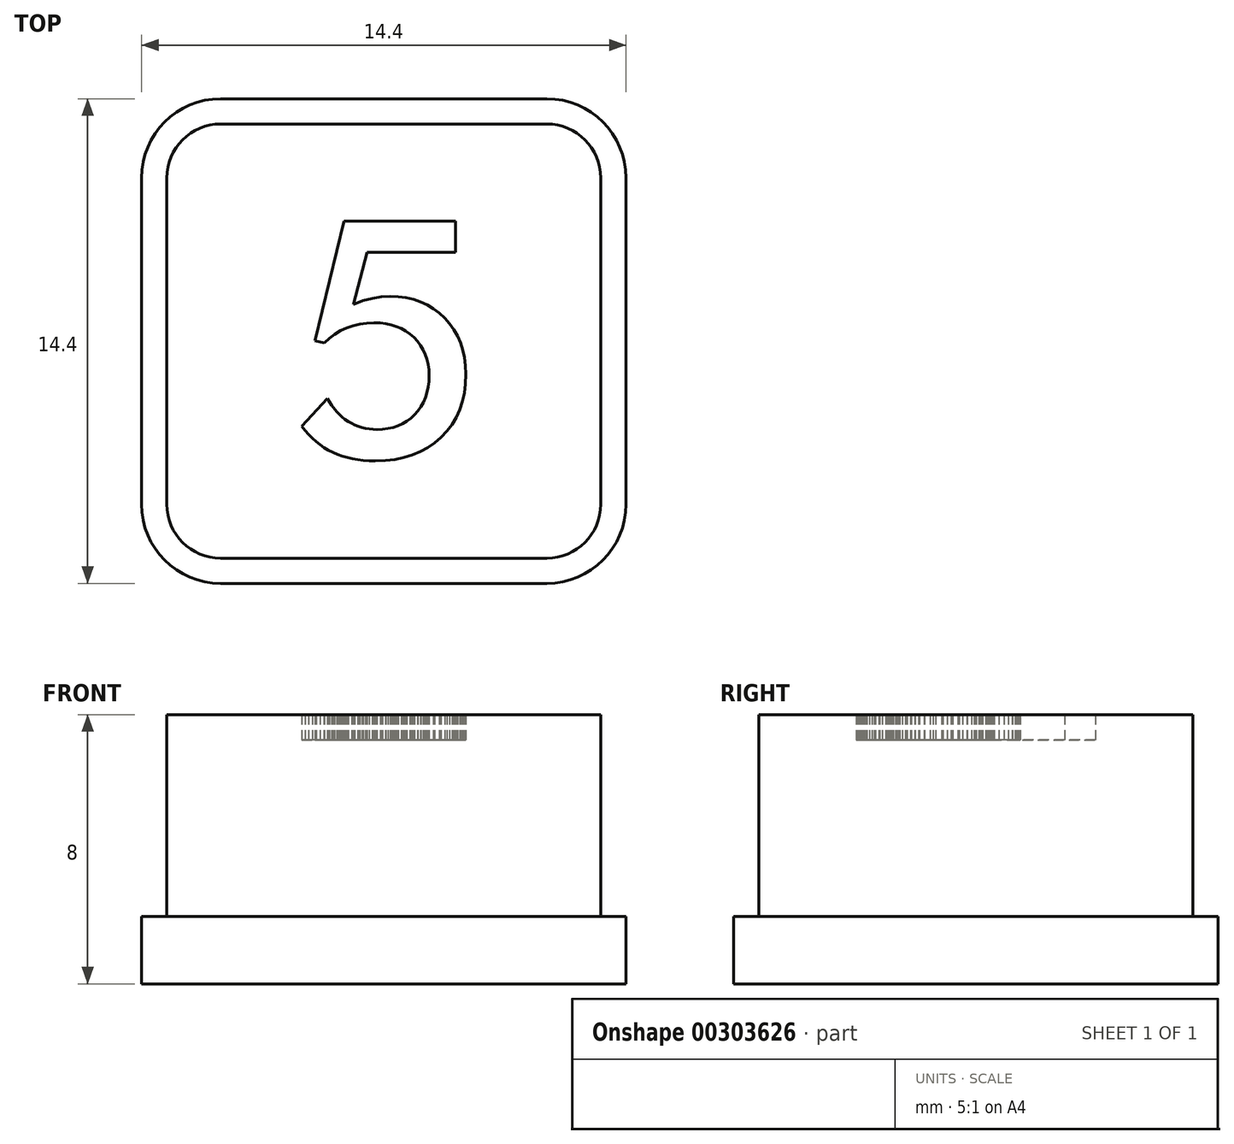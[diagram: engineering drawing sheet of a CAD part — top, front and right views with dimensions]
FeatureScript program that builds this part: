
annotation { "Feature Type Name" : "Feature", "Feature Type Description" : "" }
export const myFeature = defineFeature(function(context is Context, id is Id, definition is map)
    precondition{}
    {
        {
            var Q0;
            Q0=qCreatedBy(makeId("Top.planeOp"),FACE);
            var sketch = newSketch(context, id + "F0", { "sketchPlane" : qUnion([Q0])});
            skArc(sketch, "E0", {"start": v(4.85, -6.45) * mm, "mid": v(5.98, -5.98) * mm, "end": v(6.45, -4.85) * mm});
            skLineSegment(sketch, "E1", {"start": v(6.45, -4.85) * mm, "end": v(6.45, 4.85) * mm});
            skArc(sketch, "E2", {"start": v(6.45, 4.85) * mm, "mid": v(5.98, 5.98) * mm, "end": v(4.85, 6.45) * mm});
            skLineSegment(sketch, "E3", {"start": v(4.85, 6.45) * mm, "end": v(-4.85, 6.45) * mm});
            skArc(sketch, "E4", {"start": v(-4.85, 6.45) * mm, "mid": v(-5.98, 5.98) * mm, "end": v(-6.45, 4.85) * mm});
            skLineSegment(sketch, "E5", {"start": v(-6.45, 4.85) * mm, "end": v(-6.45, -4.85) * mm});
            skArc(sketch, "E6", {"start": v(-6.45, -4.85) * mm, "mid": v(-5.98, -5.98) * mm, "end": v(-4.85, -6.45) * mm});
            skLineSegment(sketch, "E7", {"start": v(-4.85, -6.45) * mm, "end": v(4.85, -6.45) * mm});
            skArc(sketch, "E8", {"start": v(-4.85, 7.2) * mm, "mid": v(-6.51, 6.51) * mm, "end": v(-7.2, 4.85) * mm});
            skLineSegment(sketch, "E9", {"start": v(-7.2, 4.85) * mm, "end": v(-7.2, -4.85) * mm});
            skArc(sketch, "E10", {"start": v(-7.2, -4.85) * mm, "mid": v(-6.51, -6.51) * mm, "end": v(-4.85, -7.2) * mm});
            skLineSegment(sketch, "E11", {"start": v(-4.85, -7.2) * mm, "end": v(4.85, -7.2) * mm});
            skArc(sketch, "E12", {"start": v(4.85, -7.2) * mm, "mid": v(6.51, -6.51) * mm, "end": v(7.2, -4.85) * mm});
            skLineSegment(sketch, "E13", {"start": v(7.2, -4.85) * mm, "end": v(7.2, 4.85) * mm});
            skArc(sketch, "E14", {"start": v(7.2, 4.85) * mm, "mid": v(6.51, 6.51) * mm, "end": v(4.85, 7.2) * mm});
            skLineSegment(sketch, "E15", {"start": v(4.85, 7.2) * mm, "end": v(-4.85, 7.2) * mm});
            skLineSegment(sketch, "E16", {"start": v(-1.68, -1.7) * mm, "end": v(-1.55, -1.91) * mm});
            skLineSegment(sketch, "E17", {"start": v(-1.55, -1.91) * mm, "end": v(-1.4, -2.1) * mm});
            skLineSegment(sketch, "E18", {"start": v(-1.4, -2.1) * mm, "end": v(-1.32, -2.18) * mm});
            skLineSegment(sketch, "E19", {"start": v(-1.32, -2.18) * mm, "end": v(-1.24, -2.26) * mm});
            skLineSegment(sketch, "E20", {"start": v(-1.24, -2.26) * mm, "end": v(-1.15, -2.33) * mm});
            skLineSegment(sketch, "E21", {"start": v(-1.15, -2.33) * mm, "end": v(-1.06, -2.39) * mm});
            skLineSegment(sketch, "E22", {"start": v(-1.06, -2.39) * mm, "end": v(-0.96, -2.44) * mm});
            skLineSegment(sketch, "E23", {"start": v(-0.96, -2.44) * mm, "end": v(-0.86, -2.5) * mm});
            skLineSegment(sketch, "E24", {"start": v(-0.86, -2.5) * mm, "end": v(-0.76, -2.53) * mm});
            skLineSegment(sketch, "E25", {"start": v(-0.76, -2.53) * mm, "end": v(-0.65, -2.57) * mm});
            skLineSegment(sketch, "E26", {"start": v(-0.65, -2.57) * mm, "end": v(-0.54, -2.6) * mm});
            skLineSegment(sketch, "E27", {"start": v(-0.54, -2.6) * mm, "end": v(-0.43, -2.61) * mm});
            skLineSegment(sketch, "E28", {"start": v(-0.43, -2.61) * mm, "end": v(-0.32, -2.62) * mm});
            skLineSegment(sketch, "E29", {"start": v(-0.32, -2.62) * mm, "end": v(-0.2, -2.63) * mm});
            skLineSegment(sketch, "E30", {"start": v(-0.2, -2.63) * mm, "end": v(-0.04, -2.62) * mm});
            skLineSegment(sketch, "E31", {"start": v(-0.04, -2.62) * mm, "end": v(0.12, -2.6) * mm});
            skLineSegment(sketch, "E32", {"start": v(0.12, -2.6) * mm, "end": v(0.28, -2.57) * mm});
            skLineSegment(sketch, "E33", {"start": v(0.28, -2.57) * mm, "end": v(0.42, -2.52) * mm});
            skLineSegment(sketch, "E34", {"start": v(0.42, -2.52) * mm, "end": v(0.56, -2.45) * mm});
            skLineSegment(sketch, "E35", {"start": v(0.56, -2.45) * mm, "end": v(0.69, -2.38) * mm});
            skLineSegment(sketch, "E36", {"start": v(0.69, -2.38) * mm, "end": v(0.8, -2.29) * mm});
            skLineSegment(sketch, "E37", {"start": v(0.8, -2.29) * mm, "end": v(0.92, -2.19) * mm});
            skLineSegment(sketch, "E38", {"start": v(0.92, -2.19) * mm, "end": v(1.02, -2.07) * mm});
            skLineSegment(sketch, "E39", {"start": v(1.02, -2.07) * mm, "end": v(1.1, -1.95) * mm});
            skLineSegment(sketch, "E40", {"start": v(1.1, -1.95) * mm, "end": v(1.18, -1.81) * mm});
            skLineSegment(sketch, "E41", {"start": v(1.18, -1.81) * mm, "end": v(1.24, -1.67) * mm});
            skLineSegment(sketch, "E42", {"start": v(1.24, -1.67) * mm, "end": v(1.29, -1.52) * mm});
            skLineSegment(sketch, "E43", {"start": v(1.29, -1.52) * mm, "end": v(1.32, -1.36) * mm});
            skLineSegment(sketch, "E44", {"start": v(1.32, -1.36) * mm, "end": v(1.34, -1.2) * mm});
            skLineSegment(sketch, "E45", {"start": v(1.34, -1.2) * mm, "end": v(1.35, -1.02) * mm});
            skLineSegment(sketch, "E46", {"start": v(1.35, -1.02) * mm, "end": v(1.34, -0.85) * mm});
            skLineSegment(sketch, "E47", {"start": v(1.34, -0.85) * mm, "end": v(1.32, -0.7) * mm});
            skLineSegment(sketch, "E48", {"start": v(1.32, -0.7) * mm, "end": v(1.28, -0.54) * mm});
            skLineSegment(sketch, "E49", {"start": v(1.28, -0.54) * mm, "end": v(1.24, -0.4) * mm});
            skLineSegment(sketch, "E50", {"start": v(1.24, -0.4) * mm, "end": v(1.17, -0.26) * mm});
            skLineSegment(sketch, "E51", {"start": v(1.17, -0.26) * mm, "end": v(1.1, -0.13) * mm});
            skLineSegment(sketch, "E52", {"start": v(1.1, -0.13) * mm, "end": v(1, 0) * mm});
            skLineSegment(sketch, "E53", {"start": v(1, 0) * mm, "end": v(0.9, 0.1) * mm});
            skLineSegment(sketch, "E54", {"start": v(0.9, 0.1) * mm, "end": v(0.78, 0.2) * mm});
            skLineSegment(sketch, "E55", {"start": v(0.78, 0.2) * mm, "end": v(0.65, 0.3) * mm});
            skLineSegment(sketch, "E56", {"start": v(0.65, 0.3) * mm, "end": v(0.52, 0.37) * mm});
            skLineSegment(sketch, "E57", {"start": v(0.52, 0.37) * mm, "end": v(0.37, 0.43) * mm});
            skLineSegment(sketch, "E58", {"start": v(0.37, 0.43) * mm, "end": v(0.22, 0.48) * mm});
            skLineSegment(sketch, "E59", {"start": v(0.22, 0.48) * mm, "end": v(0.06, 0.52) * mm});
            skLineSegment(sketch, "E60", {"start": v(0.06, 0.52) * mm, "end": v(-0.1, 0.54) * mm});
            skLineSegment(sketch, "E61", {"start": v(-0.1, 0.54) * mm, "end": v(-0.29, 0.54) * mm});
            skLineSegment(sketch, "E62", {"start": v(-0.29, 0.54) * mm, "end": v(-0.5, 0.53) * mm});
            skLineSegment(sketch, "E63", {"start": v(-0.5, 0.53) * mm, "end": v(-0.71, 0.5) * mm});
            skLineSegment(sketch, "E64", {"start": v(-0.71, 0.5) * mm, "end": v(-0.91, 0.46) * mm});
            skLineSegment(sketch, "E65", {"start": v(-0.91, 0.46) * mm, "end": v(-1.1, 0.4) * mm});
            skLineSegment(sketch, "E66", {"start": v(-1.1, 0.4) * mm, "end": v(-1.28, 0.3) * mm});
            skLineSegment(sketch, "E67", {"start": v(-1.28, 0.3) * mm, "end": v(-1.46, 0.2) * mm});
            skLineSegment(sketch, "E68", {"start": v(-1.46, 0.2) * mm, "end": v(-1.62, 0.08) * mm});
            skLineSegment(sketch, "E69", {"start": v(-1.62, 0.08) * mm, "end": v(-1.76, -0.05) * mm});
            skLineSegment(sketch, "E70", {"start": v(-1.76, -0.05) * mm, "end": v(-2.05, 0) * mm});
            skLineSegment(sketch, "E71", {"start": v(-2.05, 0) * mm, "end": v(-1.18, 3.56) * mm});
            skLineSegment(sketch, "E72", {"start": v(-1.18, 3.56) * mm, "end": v(2.13, 3.56) * mm});
            skLineSegment(sketch, "E73", {"start": v(2.13, 3.56) * mm, "end": v(2.13, 2.64) * mm});
            skLineSegment(sketch, "E74", {"start": v(2.13, 2.64) * mm, "end": v(-0.5, 2.64) * mm});
            skLineSegment(sketch, "E75", {"start": v(-0.5, 2.64) * mm, "end": v(-0.9, 1.1) * mm});
            skLineSegment(sketch, "E76", {"start": v(-0.9, 1.1) * mm, "end": v(-0.62, 1.2) * mm});
            skLineSegment(sketch, "E77", {"start": v(-0.62, 1.2) * mm, "end": v(-0.35, 1.27) * mm});
            skLineSegment(sketch, "E78", {"start": v(-0.35, 1.27) * mm, "end": v(-0.08, 1.31) * mm});
            skLineSegment(sketch, "E79", {"start": v(-0.08, 1.31) * mm, "end": v(0.19, 1.33) * mm});
            skLineSegment(sketch, "E80", {"start": v(0.19, 1.33) * mm, "end": v(0.43, 1.32) * mm});
            skLineSegment(sketch, "E81", {"start": v(0.43, 1.32) * mm, "end": v(0.66, 1.29) * mm});
            skLineSegment(sketch, "E82", {"start": v(0.66, 1.29) * mm, "end": v(0.88, 1.24) * mm});
            skLineSegment(sketch, "E83", {"start": v(0.88, 1.24) * mm, "end": v(1.1, 1.17) * mm});
            skLineSegment(sketch, "E84", {"start": v(1.1, 1.17) * mm, "end": v(1.29, 1.08) * mm});
            skLineSegment(sketch, "E85", {"start": v(1.29, 1.08) * mm, "end": v(1.48, 0.97) * mm});
            skLineSegment(sketch, "E86", {"start": v(1.48, 0.97) * mm, "end": v(1.65, 0.84) * mm});
            skLineSegment(sketch, "E87", {"start": v(1.65, 0.84) * mm, "end": v(1.81, 0.69) * mm});
            skLineSegment(sketch, "E88", {"start": v(1.81, 0.69) * mm, "end": v(1.96, 0.52) * mm});
            skLineSegment(sketch, "E89", {"start": v(1.96, 0.52) * mm, "end": v(2.09, 0.34) * mm});
            skLineSegment(sketch, "E90", {"start": v(2.09, 0.34) * mm, "end": v(2.2, 0.15) * mm});
            skLineSegment(sketch, "E91", {"start": v(2.2, 0.15) * mm, "end": v(2.28, -0.05) * mm});
            skLineSegment(sketch, "E92", {"start": v(2.28, -0.05) * mm, "end": v(2.35, -0.27) * mm});
            skLineSegment(sketch, "E93", {"start": v(2.35, -0.27) * mm, "end": v(2.4, -0.5) * mm});
            skLineSegment(sketch, "E94", {"start": v(2.4, -0.5) * mm, "end": v(2.43, -0.73) * mm});
            skLineSegment(sketch, "E95", {"start": v(2.43, -0.73) * mm, "end": v(2.44, -0.98) * mm});
            skLineSegment(sketch, "E96", {"start": v(2.44, -0.98) * mm, "end": v(2.43, -1.27) * mm});
            skLineSegment(sketch, "E97", {"start": v(2.43, -1.27) * mm, "end": v(2.4, -1.54) * mm});
            skLineSegment(sketch, "E98", {"start": v(2.4, -1.54) * mm, "end": v(2.34, -1.8) * mm});
            skLineSegment(sketch, "E99", {"start": v(2.34, -1.8) * mm, "end": v(2.26, -2.04) * mm});
            skLineSegment(sketch, "E100", {"start": v(2.26, -2.04) * mm, "end": v(2.15, -2.27) * mm});
            skLineSegment(sketch, "E101", {"start": v(2.15, -2.27) * mm, "end": v(2.03, -2.48) * mm});
            skLineSegment(sketch, "E102", {"start": v(2.03, -2.48) * mm, "end": v(1.88, -2.68) * mm});
            skLineSegment(sketch, "E103", {"start": v(1.88, -2.68) * mm, "end": v(1.7, -2.86) * mm});
            skLineSegment(sketch, "E104", {"start": v(1.7, -2.86) * mm, "end": v(1.52, -3.02) * mm});
            skLineSegment(sketch, "E105", {"start": v(1.52, -3.02) * mm, "end": v(1.31, -3.17) * mm});
            skLineSegment(sketch, "E106", {"start": v(1.31, -3.17) * mm, "end": v(1.09, -3.29) * mm});
            skLineSegment(sketch, "E107", {"start": v(1.09, -3.29) * mm, "end": v(0.85, -3.38) * mm});
            skLineSegment(sketch, "E108", {"start": v(0.85, -3.38) * mm, "end": v(0.6, -3.46) * mm});
            skLineSegment(sketch, "E109", {"start": v(0.6, -3.46) * mm, "end": v(0.33, -3.52) * mm});
            skLineSegment(sketch, "E110", {"start": v(0.33, -3.52) * mm, "end": v(0.05, -3.55) * mm});
            skLineSegment(sketch, "E111", {"start": v(0.05, -3.55) * mm, "end": v(-0.25, -3.56) * mm});
            skLineSegment(sketch, "E112", {"start": v(-0.25, -3.56) * mm, "end": v(-0.43, -3.56) * mm});
            skLineSegment(sketch, "E113", {"start": v(-0.43, -3.56) * mm, "end": v(-0.6, -3.54) * mm});
            skLineSegment(sketch, "E114", {"start": v(-0.6, -3.54) * mm, "end": v(-0.77, -3.52) * mm});
            skLineSegment(sketch, "E115", {"start": v(-0.77, -3.52) * mm, "end": v(-0.93, -3.5) * mm});
            skLineSegment(sketch, "E116", {"start": v(-0.93, -3.5) * mm, "end": v(-1.09, -3.46) * mm});
            skLineSegment(sketch, "E117", {"start": v(-1.09, -3.46) * mm, "end": v(-1.24, -3.42) * mm});
            skLineSegment(sketch, "E118", {"start": v(-1.24, -3.42) * mm, "end": v(-1.38, -3.37) * mm});
            skLineSegment(sketch, "E119", {"start": v(-1.38, -3.37) * mm, "end": v(-1.52, -3.3) * mm});
            skLineSegment(sketch, "E120", {"start": v(-1.52, -3.3) * mm, "end": v(-1.65, -3.24) * mm});
            skLineSegment(sketch, "E121", {"start": v(-1.65, -3.24) * mm, "end": v(-1.77, -3.17) * mm});
            skLineSegment(sketch, "E122", {"start": v(-1.77, -3.17) * mm, "end": v(-1.9, -3.08) * mm});
            skLineSegment(sketch, "E123", {"start": v(-1.9, -3.08) * mm, "end": v(-2.01, -2.99) * mm});
            skLineSegment(sketch, "E124", {"start": v(-2.01, -2.99) * mm, "end": v(-2.13, -2.89) * mm});
            skLineSegment(sketch, "E125", {"start": v(-2.13, -2.89) * mm, "end": v(-2.24, -2.78) * mm});
            skLineSegment(sketch, "E126", {"start": v(-2.24, -2.78) * mm, "end": v(-2.34, -2.66) * mm});
            skLineSegment(sketch, "E127", {"start": v(-2.34, -2.66) * mm, "end": v(-2.44, -2.53) * mm});
            skLineSegment(sketch, "E128", {"start": v(-2.44, -2.53) * mm, "end": v(-1.68, -1.7) * mm});
            skSolve(sketch);
        }
        {
            var Q0;
            Q0=makeQuery(id+"F0.imprint","IMPRINT",FACE,{"disambiguationData":[TD([[makeQuery(id+"F0.imprint","IMPRINT",EDGE,{"derivedFrom":sQuery(id+"F0.wireOp",EDGE,"E0")}),-1.0]])]});
            extrude(context, id + "F1", {"entities" : qUnion([Q0]), "depth" : 2 * mm});
        }
        {
            var Q0;
            Q0=makeQuery(id+"F0.imprint","IMPRINT",FACE,{"disambiguationData":[TD([[makeQuery(id+"F0.imprint","IMPRINT",EDGE,{"derivedFrom":sQuery(id+"F0.wireOp",EDGE,"E0")}),1.0]])]});
            extrude(context, id + "F2", {"entities" : qUnion([Q0]), "operationType" : NewBodyOperationType.ADD, "depth" : 8 * mm});
        }
        {
            var Q0;
            Q0=makeQuery(id+"F0.imprint","IMPRINT",FACE,{"disambiguationData":[TD([[makeQuery(id+"F0.imprint","IMPRINT",EDGE,{"derivedFrom":sQuery(id+"F0.wireOp",EDGE,"E16")}),-1.0]])]});
            extrude(context, id + "F3", {"entities" : qUnion([Q0]), "operationType" : NewBodyOperationType.ADD, "depth" : 7.25 * mm});
        }
    });
